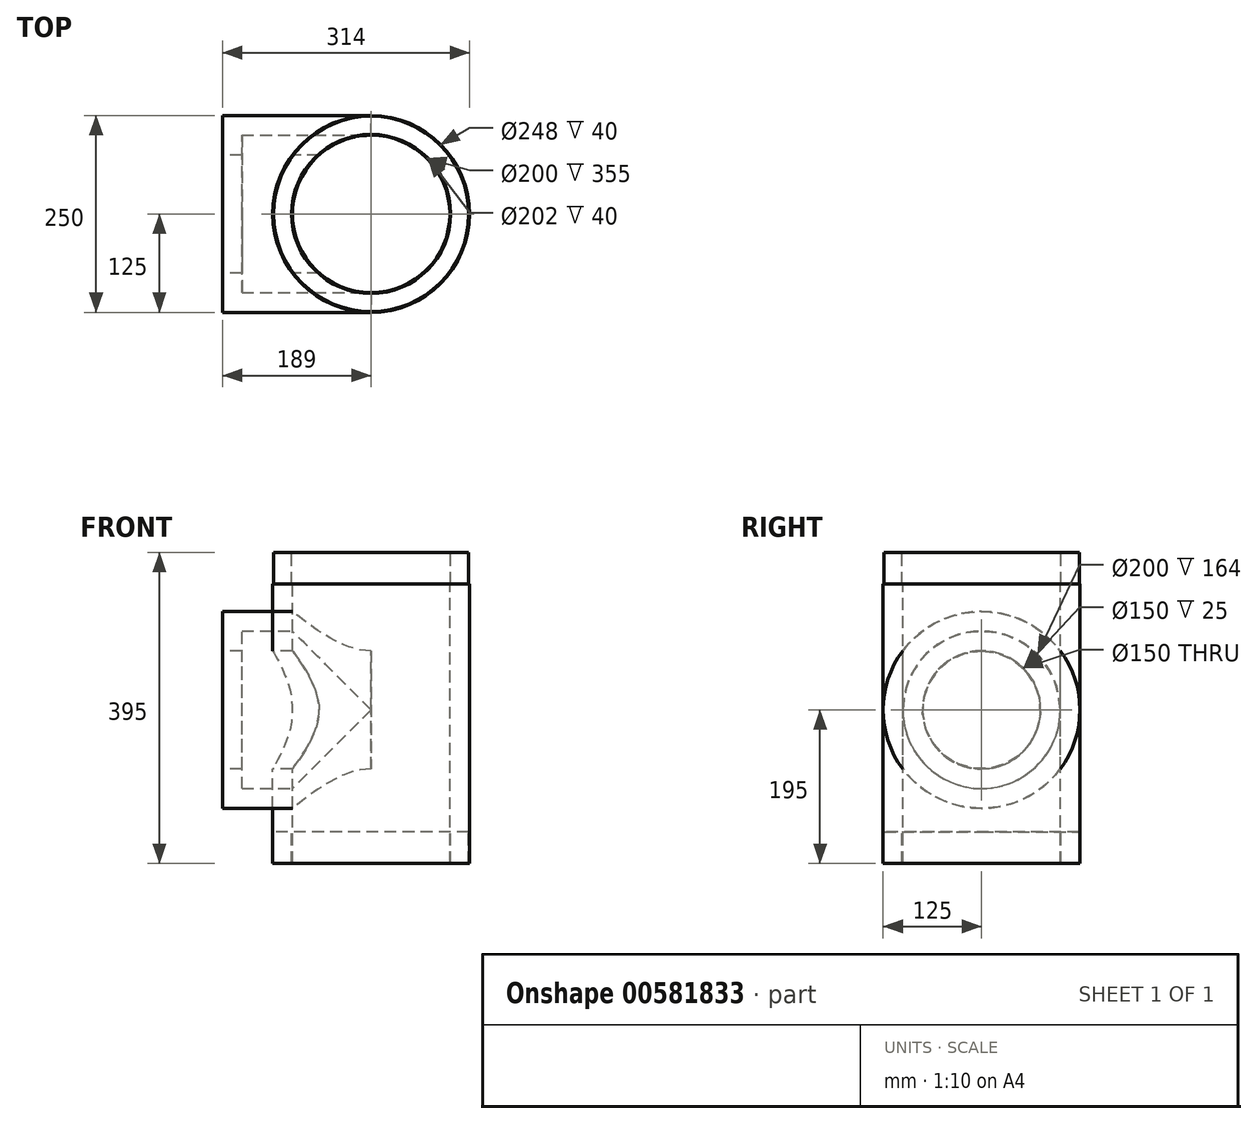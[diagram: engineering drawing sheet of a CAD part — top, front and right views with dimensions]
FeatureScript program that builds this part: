
annotation { "Feature Type Name" : "Feature", "Feature Type Description" : "" }
export const myFeature = defineFeature(function(context is Context, id is Id, definition is map)
    precondition{}
    {
        {
            var Q0;
            Q0=qCreatedBy(makeId("Front.planeOp"),FACE);
            var sketch = newSketch(context, id + "F0", { "sketchPlane" : qUnion([Q0]), "disableImprinting" : false});
            skLineSegment(sketch, "E0", {"start": v(0, 722.18) * mm, "end": v(0, -793.11) * mm, "construction": true});
            skLineSegment(sketch, "E1", {"start": v(-100, -195) * mm, "end": v(-100, 160) * mm});
            skLineSegment(sketch, "E2", {"start": v(-100, 160) * mm, "end": v(-101, 160) * mm});
            skLineSegment(sketch, "E3", {"start": v(-101, 160) * mm, "end": v(-101, 200) * mm});
            skLineSegment(sketch, "E4", {"start": v(-101, 200) * mm, "end": v(-124, 200) * mm});
            skLineSegment(sketch, "E5", {"start": v(-124, 200) * mm, "end": v(-124, 160) * mm});
            skLineSegment(sketch, "E6", {"start": v(-124, 160) * mm, "end": v(-125, 160) * mm});
            skLineSegment(sketch, "E7", {"start": v(-125, 160) * mm, "end": v(-125, -195) * mm});
            skLineSegment(sketch, "E8", {"start": v(-125, -195) * mm, "end": v(-124, -195) * mm});
            skLineSegment(sketch, "E9", {"start": v(-124, -195) * mm, "end": v(-124, -155) * mm});
            skLineSegment(sketch, "E10", {"start": v(-124, -155) * mm, "end": v(-101, -155) * mm});
            skLineSegment(sketch, "E11", {"start": v(-101, -155) * mm, "end": v(-101, -195) * mm});
            skLineSegment(sketch, "E12", {"start": v(-101, -195) * mm, "end": v(-100, -195) * mm});
            skLineSegment(sketch, "E13", {"start": v(0, 0) * mm, "end": v(-328, 0) * mm, "construction": true});
            skLineSegment(sketch, "E14", {"start": v(0, -100) * mm, "end": v(-189, -100) * mm});
            skLineSegment(sketch, "E15", {"start": v(-189, -100) * mm, "end": v(-189, -125) * mm});
            skLineSegment(sketch, "E16", {"start": v(-189, -125) * mm, "end": v(0, -125) * mm});
            skLineSegment(sketch, "E17", {"start": v(0, -125) * mm, "end": v(0, -100) * mm});
            skLineSegment(sketch, "E18", {"start": v(-189, -100) * mm, "end": v(-189, 0) * mm});
            skLineSegment(sketch, "E19", {"start": v(-189, 0) * mm, "end": v(-164, 0) * mm});
            skLineSegment(sketch, "E20", {"start": v(-164, 0) * mm, "end": v(-164, -100) * mm});
            skSolve(sketch);
        }
        {
            var Q0;
            {var subQ0=sQuery(id+"F0.wireOp",EDGE,"E2");Q0=makeQuery(id+"F0.imprint","IMPRINT",FACE,{"disambiguationData":[TD([[makeQuery(id+"F0.imprint","IMPRINT",EDGE,{"derivedFrom":subQ0}),1.0]])]});}
            var Q1;
            {var subQ0=sQuery(id+"F0.wireOp",EDGE,"E16");var subQ1=sQuery(id+"F0.wireOp",EDGE,"E1");var subQ2=makeQuery(id+"F0.imprint","INTERSECT",VERTEX,{"derivedFrom":[subQ1,subQ0]});Q1=makeQuery(id+"F0.imprint","IMPRINT",FACE,{"disambiguationData":[TD([[makeQuery(id+"F0.imprint","IMPRINT",EDGE,{"disambiguationData":[TD([[subQ2,-1.0]])],"derivedFrom":subQ1}),1.0]])]});}
            var Q2;
            {var subQ0=sQuery(id+"F0.wireOp",EDGE,"E8");Q2=makeQuery(id+"F0.imprint","IMPRINT",FACE,{"disambiguationData":[TD([[makeQuery(id+"F0.imprint","IMPRINT",EDGE,{"derivedFrom":subQ0}),1.0]])]});}
            var Q3;
            Q3=sQuery(id+"F0.wireOp",EDGE,"E0");
            revolve(context, id + "F1", {"entities" : qUnion([Q0, Q1, Q2]), "axis" : qUnion([Q3]), "revolveType" : RevolveType.FULL});
        }
        {
            var Q0;
            {var subQ0=sQuery(id+"F0.wireOp",EDGE,"E18");Q0=makeQuery(id+"F0.imprint","IMPRINT",FACE,{"disambiguationData":[TD([[makeQuery(id+"F0.imprint","IMPRINT",EDGE,{"derivedFrom":subQ0}),-1.0]])]});}
            var Q1;
            {var subQ0=sQuery(id+"F0.wireOp",EDGE,"E15");Q1=makeQuery(id+"F0.imprint","IMPRINT",FACE,{"disambiguationData":[TD([[makeQuery(id+"F0.imprint","IMPRINT",EDGE,{"derivedFrom":subQ0}),1.0]])]});}
            var Q2;
            {var subQ0=sQuery(id+"F0.wireOp",EDGE,"E16");var subQ1=sQuery(id+"F0.wireOp",EDGE,"E1");var subQ2=makeQuery(id+"F0.imprint","INTERSECT",VERTEX,{"derivedFrom":[subQ1,subQ0]});Q2=makeQuery(id+"F0.imprint","IMPRINT",FACE,{"disambiguationData":[TD([[makeQuery(id+"F0.imprint","IMPRINT",EDGE,{"disambiguationData":[TD([[subQ2,-1.0]])],"derivedFrom":subQ1}),1.0]])]});}
            var Q3;
            {var subQ5=sQuery(id+"F0.wireOp",EDGE,"E17");Q3=makeQuery(id+"F0.imprint","IMPRINT",FACE,{"disambiguationData":[TD([[makeQuery(id+"F0.imprint","IMPRINT",EDGE,{"derivedFrom":subQ5}),1.0]])]});}
            var Q4;
            Q4=sQuery(id+"F0.wireOp",EDGE,"E13");
            revolve(context, id + "F2", {"entities" : qUnion([Q0, Q1, Q2, Q3]), "axis" : qUnion([Q4]), "revolveType" : RevolveType.FULL});
        }
        {
            var Q0;
            Q0=makeQuery(id+"F2.opRevolve","SWEPT_FACE",FACE,{"disambiguationData":[OSD([sQuery(id+"F0.wireOp",EDGE,"E15"),sQuery(id+"F0.wireOp",EDGE,"E18")])]});
            var sketch = newSketch(context, id + "F3", { "sketchPlane" : qUnion([Q0])});
            skCircle(sketch, "E21", {"center": v(0, 0) * mm, "radius": 75 * mm});
            skSolve(sketch);
        }
        {
            var Q0;
            Q0=qSketchRegion(id+"F3",true);
            var Q1;
            Q1=makeQuery(id+"F2.opRevolve","SWEPT_FACE",FACE,{"disambiguationData":[OSD([sQuery(id+"F0.wireOp",EDGE,"E17")])]});
            extrude(context, id + "F4", {"entities" : qUnion([Q0]), "operationType" : NewBodyOperationType.REMOVE, "endBound" : BoundingType.UP_TO_SURFACE, "oppositeDirection" : true, "endBoundEntityFace" : qUnion([Q1]), "offsetDistance" : 25 * mm, "depth" : 600 * mm});
        }
        {
            var Q0;
            Q0=makeQuery(id+"F1.opRevolve","SWEPT_FACE",FACE,{"disambiguationData":[OSD([sQuery(id+"F0.wireOp",EDGE,"E4")])]});
            var sketch = newSketch(context, id + "F5", { "sketchPlane" : qUnion([Q0])});
            skCircle(sketch, "E22", {"center": v(0, 0) * mm, "radius": 100 * mm});
            skSolve(sketch);
        }
        {
            var Q0;
            Q0=qSketchRegion(id+"F5",true);
            extrude(context, id + "F6", {"entities" : qUnion([Q0]), "operationType" : NewBodyOperationType.REMOVE, "oppositeDirection" : true, "depth" : 1200 * mm});
        }
    });
